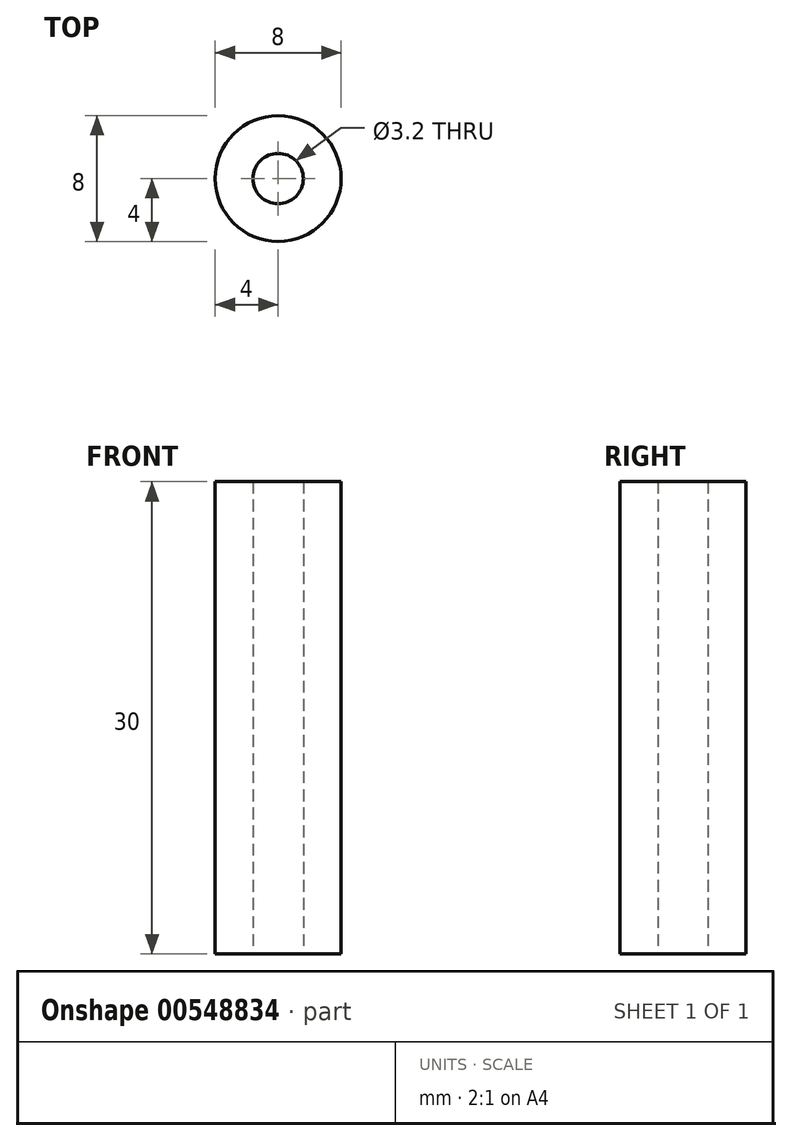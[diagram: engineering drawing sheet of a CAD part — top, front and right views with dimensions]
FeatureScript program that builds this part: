
annotation { "Feature Type Name" : "Feature", "Feature Type Description" : "" }
export const myFeature = defineFeature(function(context is Context, id is Id, definition is map)
    precondition{}
    {
        {
            var Q0;
            Q0=qCreatedBy(makeId("Top.planeOp"),FACE);
            var sketch = newSketch(context, id + "F0", { "sketchPlane" : qUnion([Q0])});
            skCircle(sketch, "E0", {"center": v(0, 0) * mm, "radius": 4 * mm});
            skCircle(sketch, "E1", {"center": v(0, 0) * mm, "radius": 1.6 * mm});
            skSolve(sketch);
        }
        {
            var Q0;
            Q0 = qSketchRegion(id + "F0", true);
            extrude(context, id + "F1", {"entities" : qUnion([Q0]), "depth" : 30 * mm, "offsetDistance" : 25 * mm});
        }
    });
